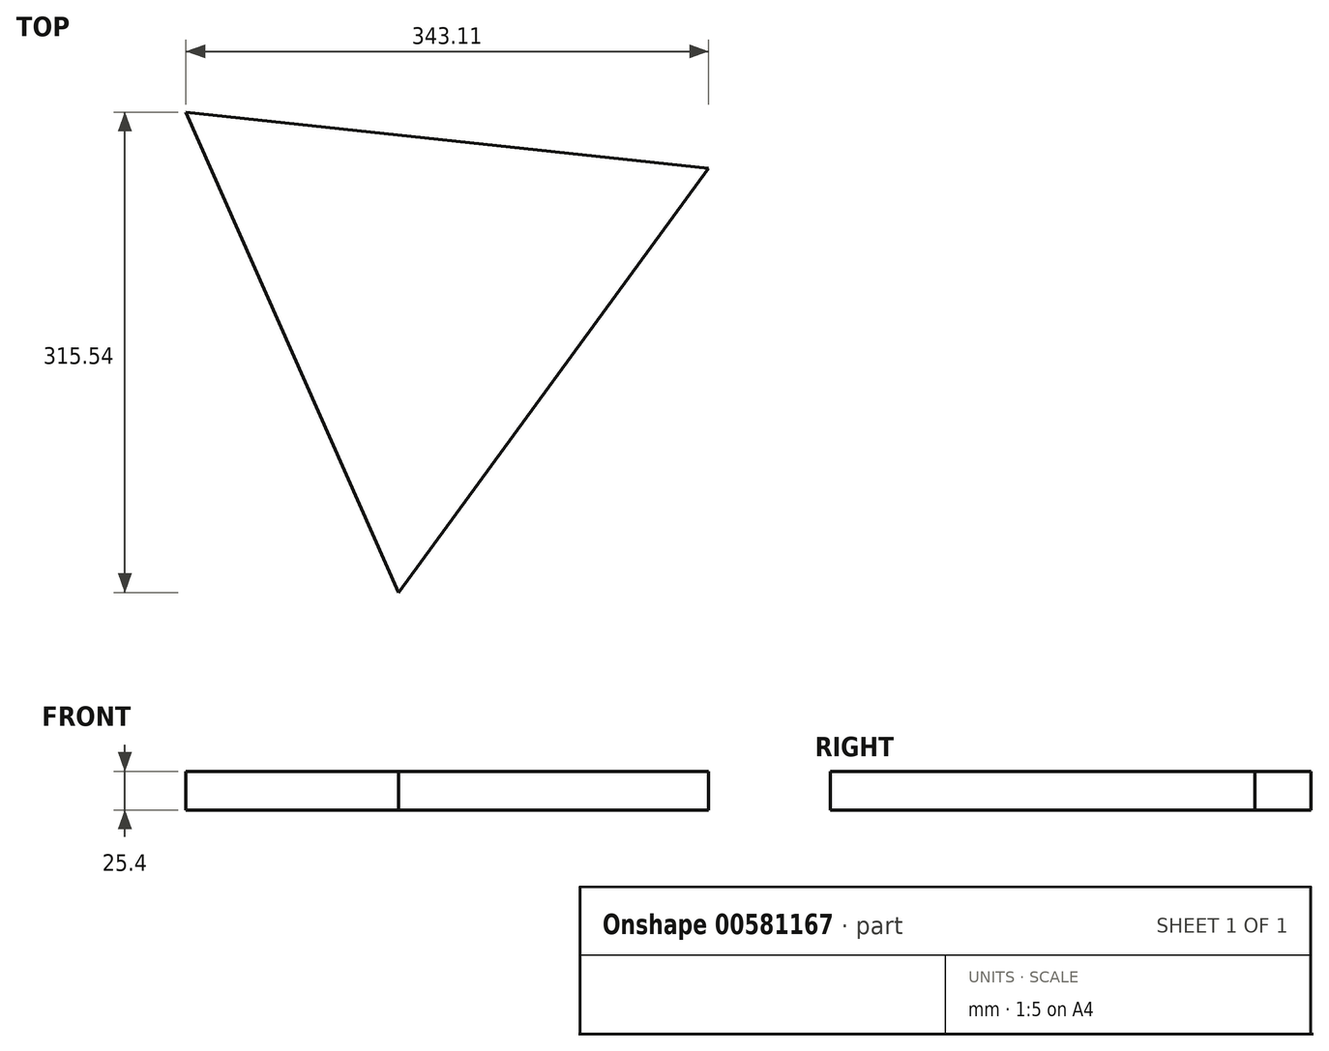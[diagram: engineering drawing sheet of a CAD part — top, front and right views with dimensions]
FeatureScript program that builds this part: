
annotation { "Feature Type Name" : "Feature", "Feature Type Description" : "" }
export const myFeature = defineFeature(function(context is Context, id is Id, definition is map)
    precondition{}
    {
        {
            var Q0;
            Q0=qCreatedBy(makeId("Top.planeOp"),FACE);
            var sketch = newSketch(context, id + "F0", { "sketchPlane" : qUnion([Q0])});
            skCircle(sketch, "E0.cCircle", {"center": v(-181, -150.26) * mm, "radius": 99.61 * mm, "construction": true});
            skLineSegment(sketch, "E0.0", {"start": v(1.18, -69.6) * mm, "end": v(-202.24, -348.35) * mm});
            skLineSegment(sketch, "E0.1", {"start": v(-202.24, -348.35) * mm, "end": v(-341.93, -32.81) * mm});
            skLineSegment(sketch, "E0.2", {"start": v(-341.93, -32.81) * mm, "end": v(1.18, -69.6) * mm});
            skPoint(sketch, "E0.0.midPoint", {"position": v(-100.53, -208.98) * mm});
            skSolve(sketch);
        }
        {
            var Q0;
            Q0 = qSketchRegion(id + "F0", true);
            extrude(context, id + "F1", {"entities" : qUnion([Q0]), "depth" : 25.4 * mm, "offsetDistance" : 25.4 * mm});
        }
    });
